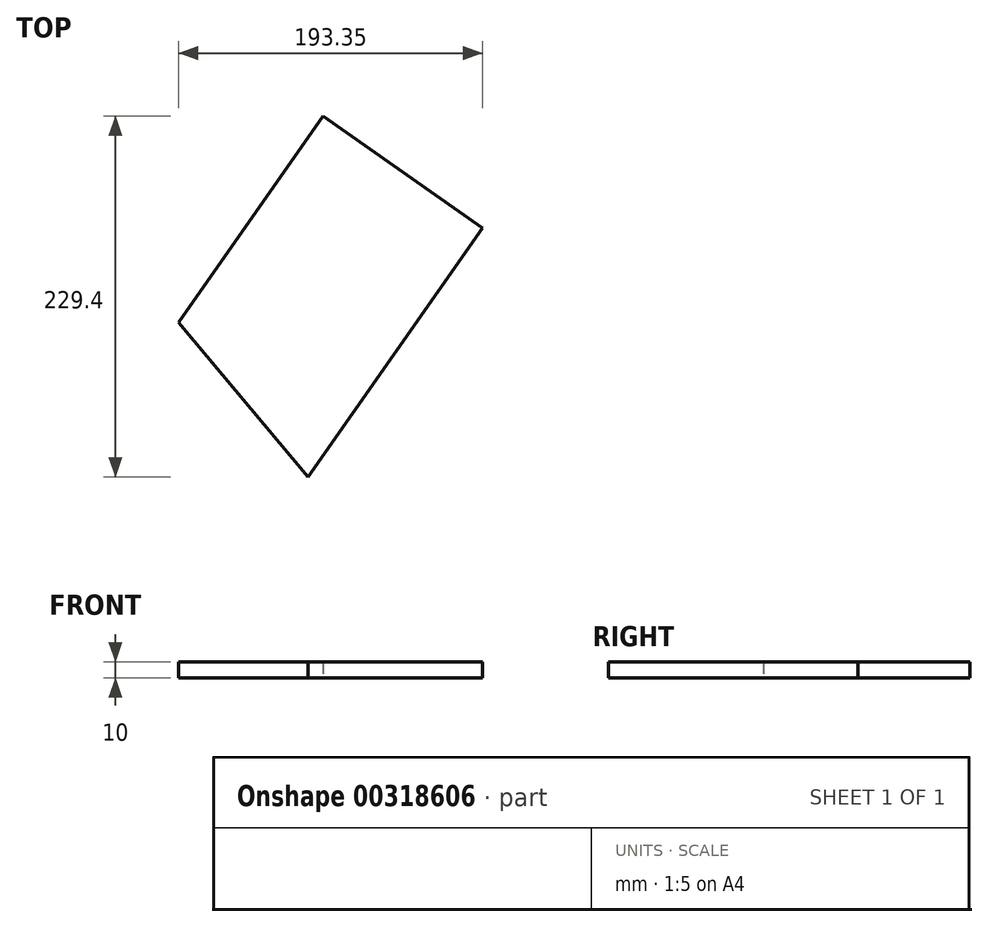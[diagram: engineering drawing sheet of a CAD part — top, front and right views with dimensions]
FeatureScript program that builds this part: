
annotation { "Feature Type Name" : "Feature", "Feature Type Description" : "" }
export const myFeature = defineFeature(function(context is Context, id is Id, definition is map)
    precondition{}
    {
        {
            var Q0;
            Q0=qCreatedBy(makeId("Top.planeOp"),FACE);
            var sketch = newSketch(context, id + "F0", { "sketchPlane" : qUnion([Q0])});
            skLineSegment(sketch, "E0", {"start": v(0, 0) * mm, "end": v(0, -158.28) * mm, "construction": true});
            skLineSegment(sketch, "E1", {"start": v(0, -158.28) * mm, "end": v(-110.83, -158.28) * mm, "construction": true});
            skLineSegment(sketch, "E2", {"start": v(-110.83, -158.28) * mm, "end": v(0, 0) * mm});
            skLineSegment(sketch, "E3", {"start": v(0, 0) * mm, "end": v(-101.57, 71.12) * mm});
            skLineSegment(sketch, "E4", {"start": v(-101.57, 71.12) * mm, "end": v(-193.35, -59.94) * mm});
            skLineSegment(sketch, "E5", {"start": v(-193.35, -59.94) * mm, "end": v(-110.83, -158.28) * mm});
            skSolve(sketch);
        }
        {
            var Q0;
            Q0=makeQuery(id+"F0.imprint","IMPRINT",FACE,{"disambiguationData":[TD([[makeQuery(id+"F0.imprint","IMPRINT",EDGE,{"derivedFrom":sQuery(id+"F0.wireOp",EDGE,"E2")}),1.0]])]});
            extrude(context, id + "F1", {"entities" : qUnion([Q0]), "depth" : 10 * mm});
        }
    });
